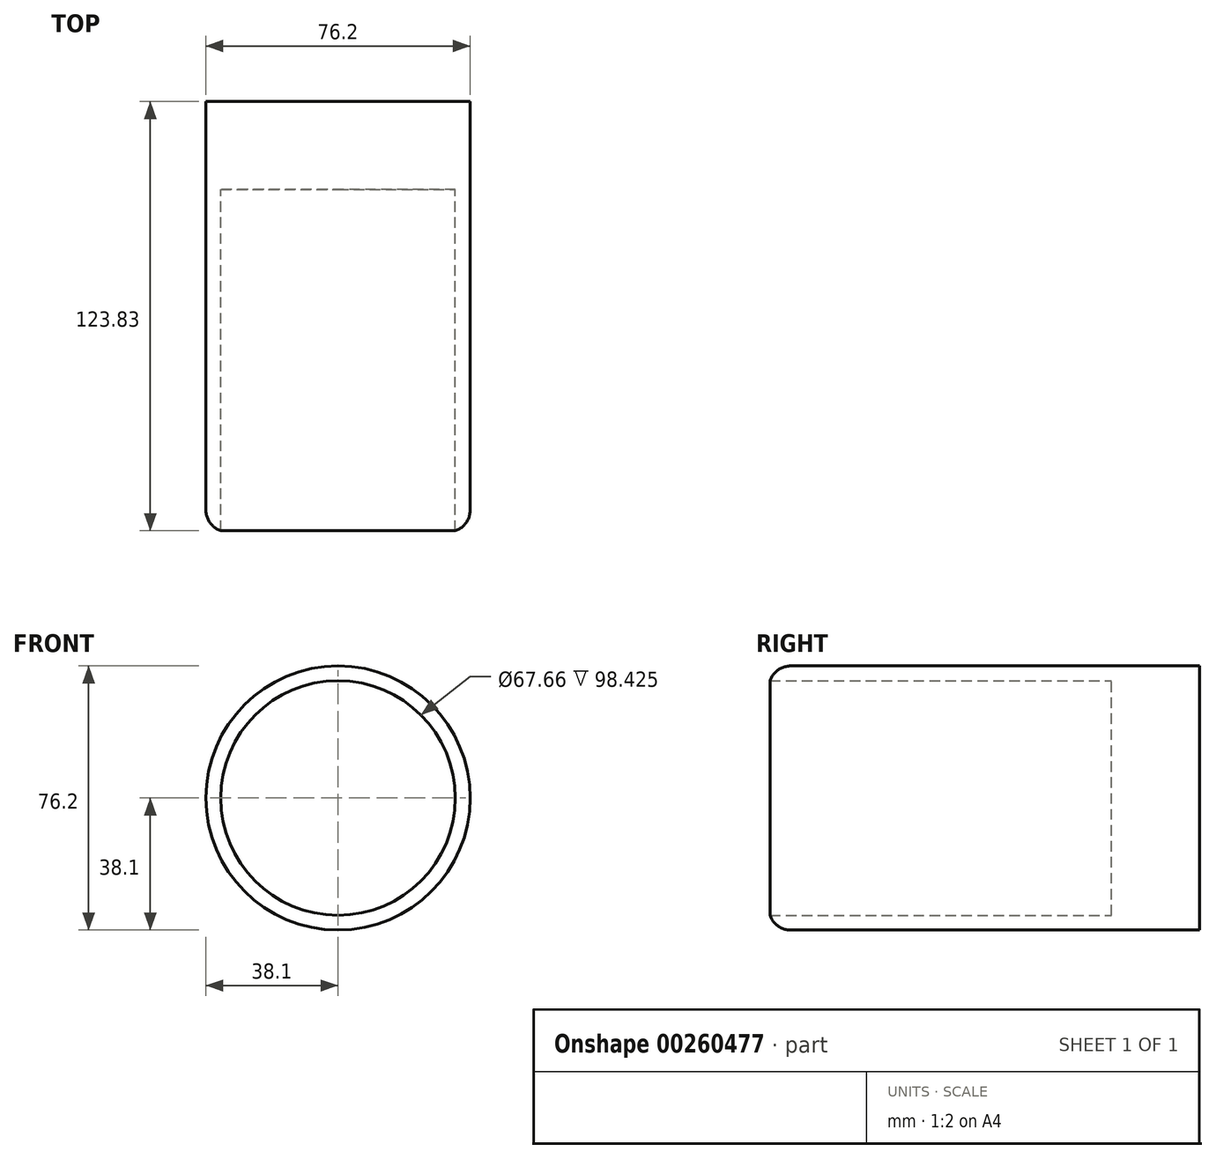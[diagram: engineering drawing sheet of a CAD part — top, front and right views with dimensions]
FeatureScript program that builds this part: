
annotation { "Feature Type Name" : "Feature", "Feature Type Description" : "" }
export const myFeature = defineFeature(function(context is Context, id is Id, definition is map)
    precondition{}
    {
        {
            var Q0;
            Q0=qCreatedBy(makeId("Front.planeOp"),FACE);
            var sketch = newSketch(context, id + "F0", { "sketchPlane" : qUnion([Q0])});
            skCircle(sketch, "E0", {"center": v(0, 0) * mm, "radius": 38.1 * mm});
            skCircle(sketch, "E1", {"center": v(0, 0) * mm, "radius": 31.75 * mm});
            skCircle(sketch, "E2", {"center": v(0, 0) * mm, "radius": 33.83 * mm});
            skSolve(sketch);
        }
        {
            var Q0;
            Q0 = qSketchRegion(id + "F0", true);
            extrude(context, id + "F1", {"entities" : qUnion([Q0]), "depth" : 123.82 * mm});
        }
        {
            var Q0;
            Q0 = qSketchRegion(id + "F0", true);
            extrude(context, id + "F2", {"entities" : qUnion([Q0]), "operationType" : NewBodyOperationType.ADD, "depth" : 9.52 * mm});
        }
        {
            var Q0;
            Q0=makeQuery(id+"F1.opExtrude","CAP_EDGE",EDGE,{"disambiguationData":[OSD([sQuery(id+"F0.wireOp",EDGE,"E0")])],"isStart":false});
            fillet(context, id + "F3", {"entities" : qUnion([Q0]), "radius" : 6.35 * mm, "tangentPropagation" : true, "allowEdgeOverflow" : false});
        }
        {
            var Q0;
            Q0 = qSketchRegion(id + "F0", true);
            extrude(context, id + "F4", {"entities" : qUnion([Q0]), "operationType" : NewBodyOperationType.ADD, "depth" : 12.7 * mm});
        }
        {
            var Q0;
            Q0=qCreatedBy(makeId("Front.planeOp"),FACE);
            var sketch = newSketch(context, id + "F5", { "sketchPlane" : qUnion([Q0])});
            skCircle(sketch, "E3", {"center": v(0, 0) * mm, "radius": 35.78 * mm});
            skSolve(sketch);
        }
        {
            var Q0;
            Q0 = qSketchRegion(id + "F5", true);
            extrude(context, id + "F6", {"entities" : qUnion([Q0]), "operationType" : NewBodyOperationType.ADD, "depth" : 25.4 * mm});
        }
    });
